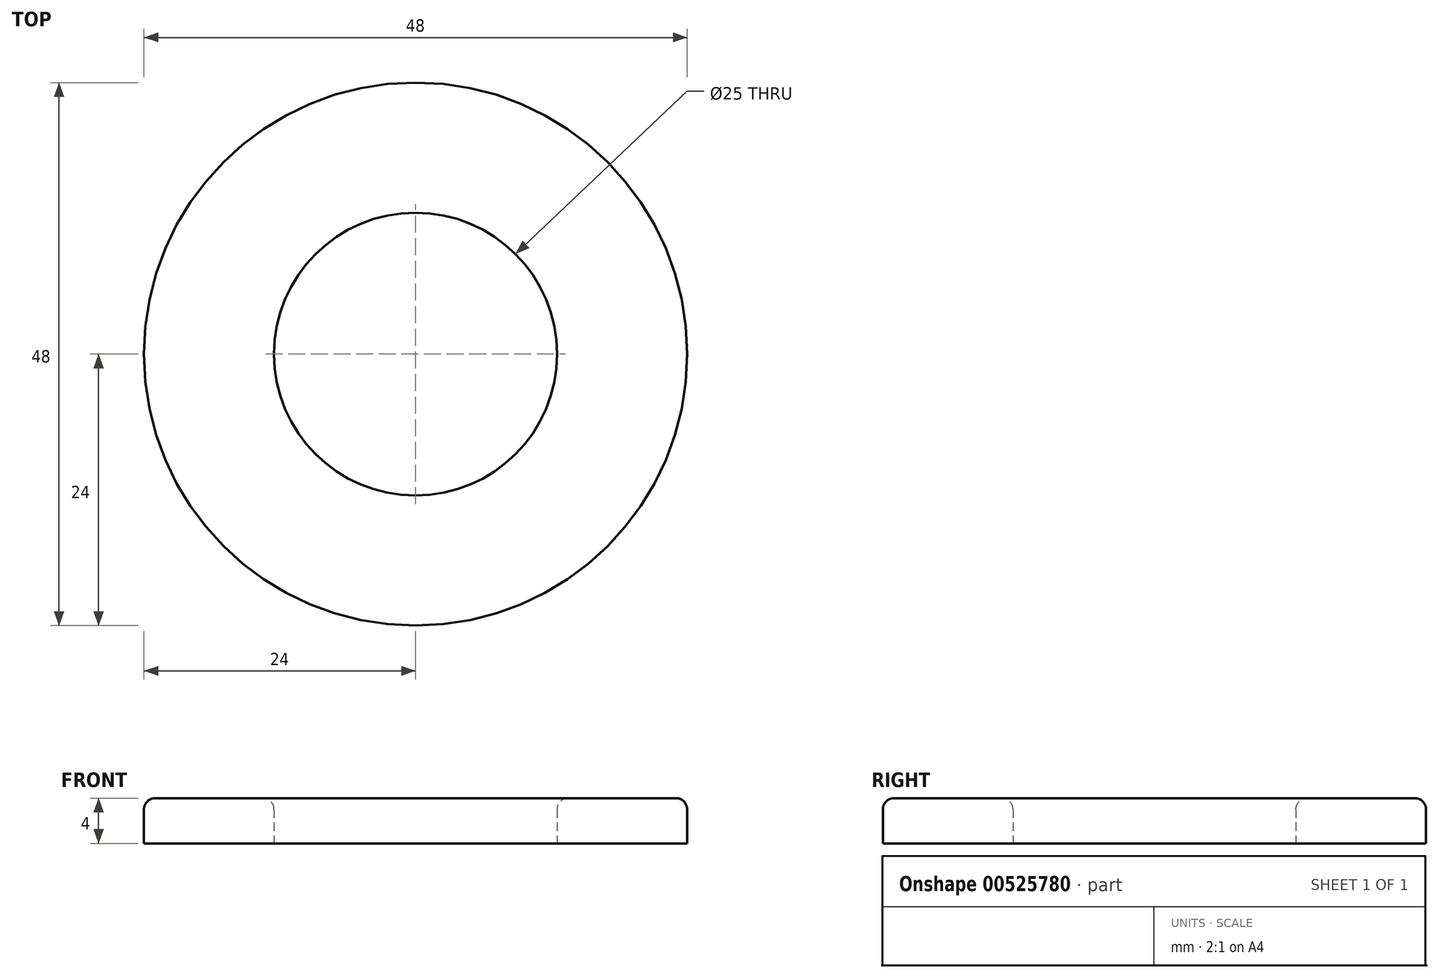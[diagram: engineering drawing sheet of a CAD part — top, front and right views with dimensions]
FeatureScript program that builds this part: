
annotation { "Feature Type Name" : "Feature", "Feature Type Description" : "" }
export const myFeature = defineFeature(function(context is Context, id is Id, definition is map)
    precondition{}
    {
        {
            var Q0;
            Q0=qCreatedBy(makeId("Top.planeOp"),FACE);
            var sketch = newSketch(context, id + "F0", { "sketchPlane" : qUnion([Q0])});
            skCircle(sketch, "E0", {"center": v(0, 0) * mm, "radius": 24 * mm});
            skCircle(sketch, "E1", {"center": v(0, 0) * mm, "radius": 12.5 * mm});
            skSolve(sketch);
        }
        {
            var Q0;
            Q0=makeQuery(id+"F0.imprint","IMPRINT",FACE,{"disambiguationData":[TD([[makeQuery(id+"F0.imprint","IMPRINT",EDGE,{"derivedFrom":sQuery(id+"F0.wireOp",EDGE,"E0")}),1.0]])]});
            extrude(context, id + "F1", {"entities" : qUnion([Q0]), "depth" : 4 * mm, "offsetDistance" : 25 * mm});
        }
        {
            var Q0;
            Q0=makeQuery(id+"F1.opExtrude","CAP_FACE",FACE,{"disambiguationData":[OSD([sQuery(id+"F0.wireOp",EDGE,"E0"),sQuery(id+"F0.wireOp",EDGE,"E1")])],"isStart":false});
            fillet(context, id + "F2", {"entities" : qUnion([Q0]), "radius" : 1 * mm, "tangentPropagation" : true, "allowEdgeOverflow" : false});
        }
    });
